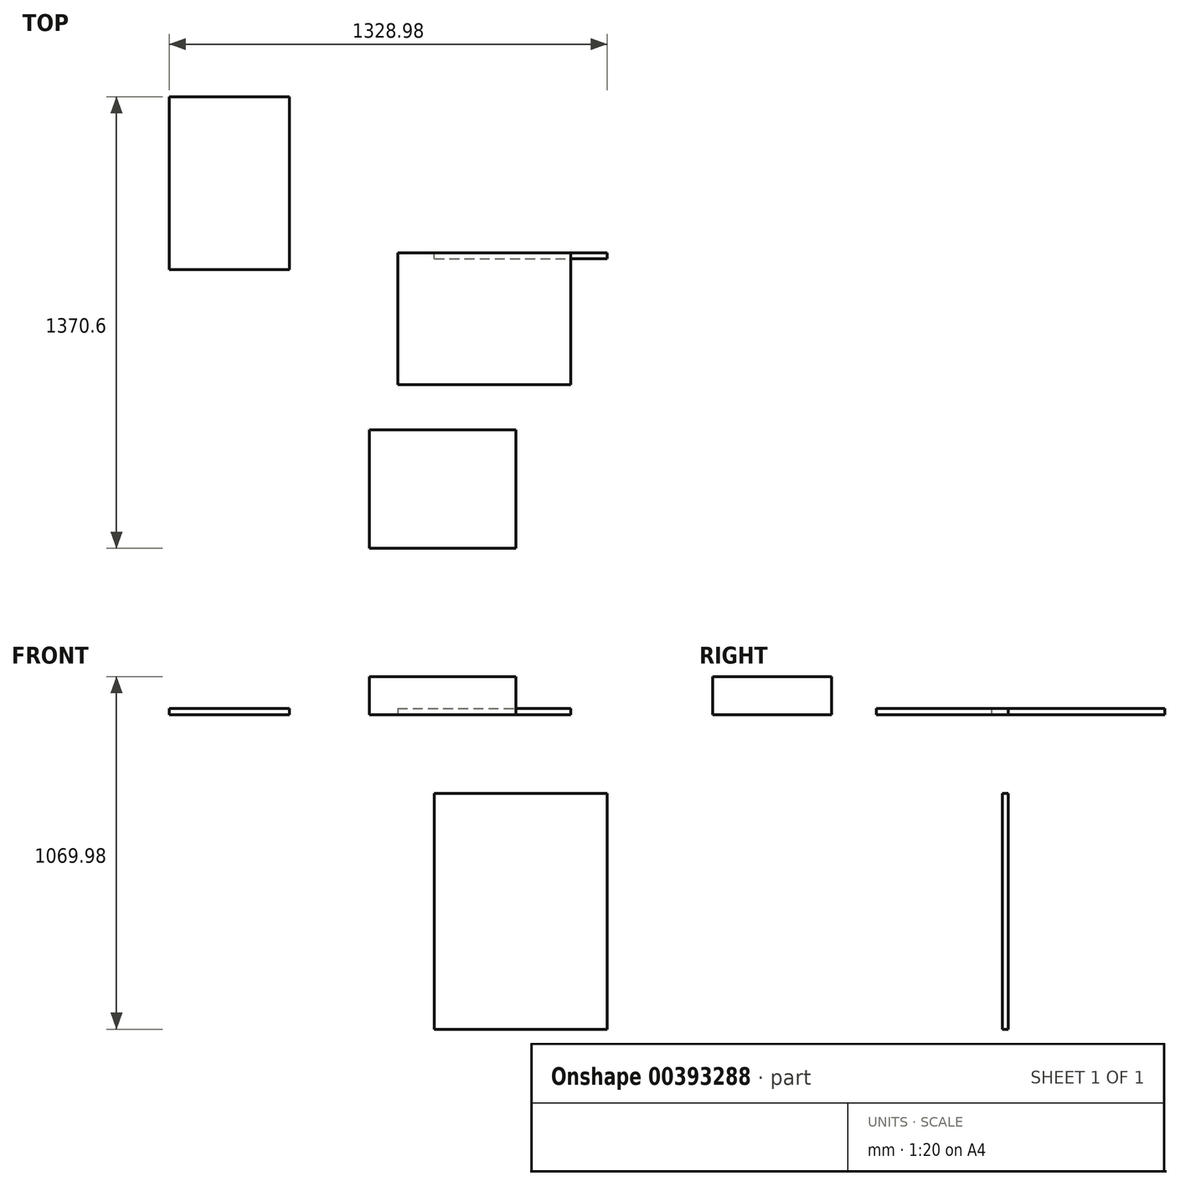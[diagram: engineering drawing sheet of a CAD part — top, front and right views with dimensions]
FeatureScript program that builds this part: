
annotation { "Feature Type Name" : "Feature", "Feature Type Description" : "" }
export const myFeature = defineFeature(function(context is Context, id is Id, definition is map)
    precondition{}
    {
        {
            var Q0;
            Q0=qCreatedBy(makeId("Top.planeOp"),FACE);
            var sketch = newSketch(context, id + "F0", { "sketchPlane" : qUnion([Q0])});
            skLineSegment(sketch, "E0", {"start": v(0, 0) * mm, "end": v(525, 0) * mm});
            skLineSegment(sketch, "E1", {"start": v(525, 0) * mm, "end": v(525, -400) * mm});
            skLineSegment(sketch, "E2", {"start": v(0, 0) * mm, "end": v(0, -400) * mm});
            skLineSegment(sketch, "E3", {"start": v(0, -400) * mm, "end": v(525, -400) * mm});
            skSolve(sketch);
        }
        {
            var Q0;
            Q0=qSketchRegion(id+"F0",true);
            extrude(context, id + "F1", {"entities" : qUnion([Q0]), "depth" : 18 * mm});
        }
        {
            var Q0;
            Q0=qCreatedBy(makeId("Front.planeOp"),FACE);
            var sketch = newSketch(context, id + "F2", { "sketchPlane" : qUnion([Q0])});
            skLineSegment(sketch, "E4.bottom", {"start": v(111.04, -238.98) * mm, "end": v(636.04, -238.98) * mm});
            skLineSegment(sketch, "E4.top", {"start": v(111.04, -954.98) * mm, "end": v(636.04, -954.98) * mm});
            skLineSegment(sketch, "E4.left", {"start": v(111.04, -238.98) * mm, "end": v(111.04, -954.98) * mm});
            skLineSegment(sketch, "E4.right", {"start": v(636.04, -238.98) * mm, "end": v(636.04, -954.98) * mm});
            skSolve(sketch);
        }
        {
            var Q0;
            Q0=qSketchRegion(id+"F2",true);
            extrude(context, id + "F3", {"entities" : qUnion([Q0]), "depth" : 18 * mm});
        }
        {
            var Q0;
            Q0=qCreatedBy(makeId("Top.planeOp"),FACE);
            var sketch = newSketch(context, id + "F4", { "sketchPlane" : qUnion([Q0])});
            skLineSegment(sketch, "E5.bottom", {"start": v(-328.94, 474.2) * mm, "end": v(-692.94, 474.2) * mm});
            skLineSegment(sketch, "E5.top", {"start": v(-328.94, -50.8) * mm, "end": v(-692.94, -50.8) * mm});
            skLineSegment(sketch, "E5.left", {"start": v(-328.94, 474.2) * mm, "end": v(-328.94, -50.8) * mm});
            skLineSegment(sketch, "E5.right", {"start": v(-692.94, 474.2) * mm, "end": v(-692.94, -50.8) * mm});
            skSolve(sketch);
        }
        {
            var Q0;
            Q0=qSketchRegion(id+"F4",true);
            extrude(context, id + "F5", {"entities" : qUnion([Q0]), "depth" : 18 * mm});
        }
        {
            var Q0;
            Q0=qCreatedBy(makeId("Top.planeOp"),FACE);
            var sketch = newSketch(context, id + "F6", { "sketchPlane" : qUnion([Q0])});
            skLineSegment(sketch, "E6.bottom", {"start": v(359.09, -536.4) * mm, "end": v(-85.91, -536.4) * mm});
            skLineSegment(sketch, "E6.top", {"start": v(359.09, -896.4) * mm, "end": v(-85.91, -896.4) * mm});
            skLineSegment(sketch, "E6.left", {"start": v(359.09, -536.4) * mm, "end": v(359.09, -896.4) * mm});
            skLineSegment(sketch, "E6.right", {"start": v(-85.91, -536.4) * mm, "end": v(-85.91, -896.4) * mm});
            skSolve(sketch);
        }
        {
            var Q0;
            Q0=qSketchRegion(id+"F6",true);
            extrude(context, id + "F7", {"entities" : qUnion([Q0]), "depth" : 115 * mm});
        }
    });
